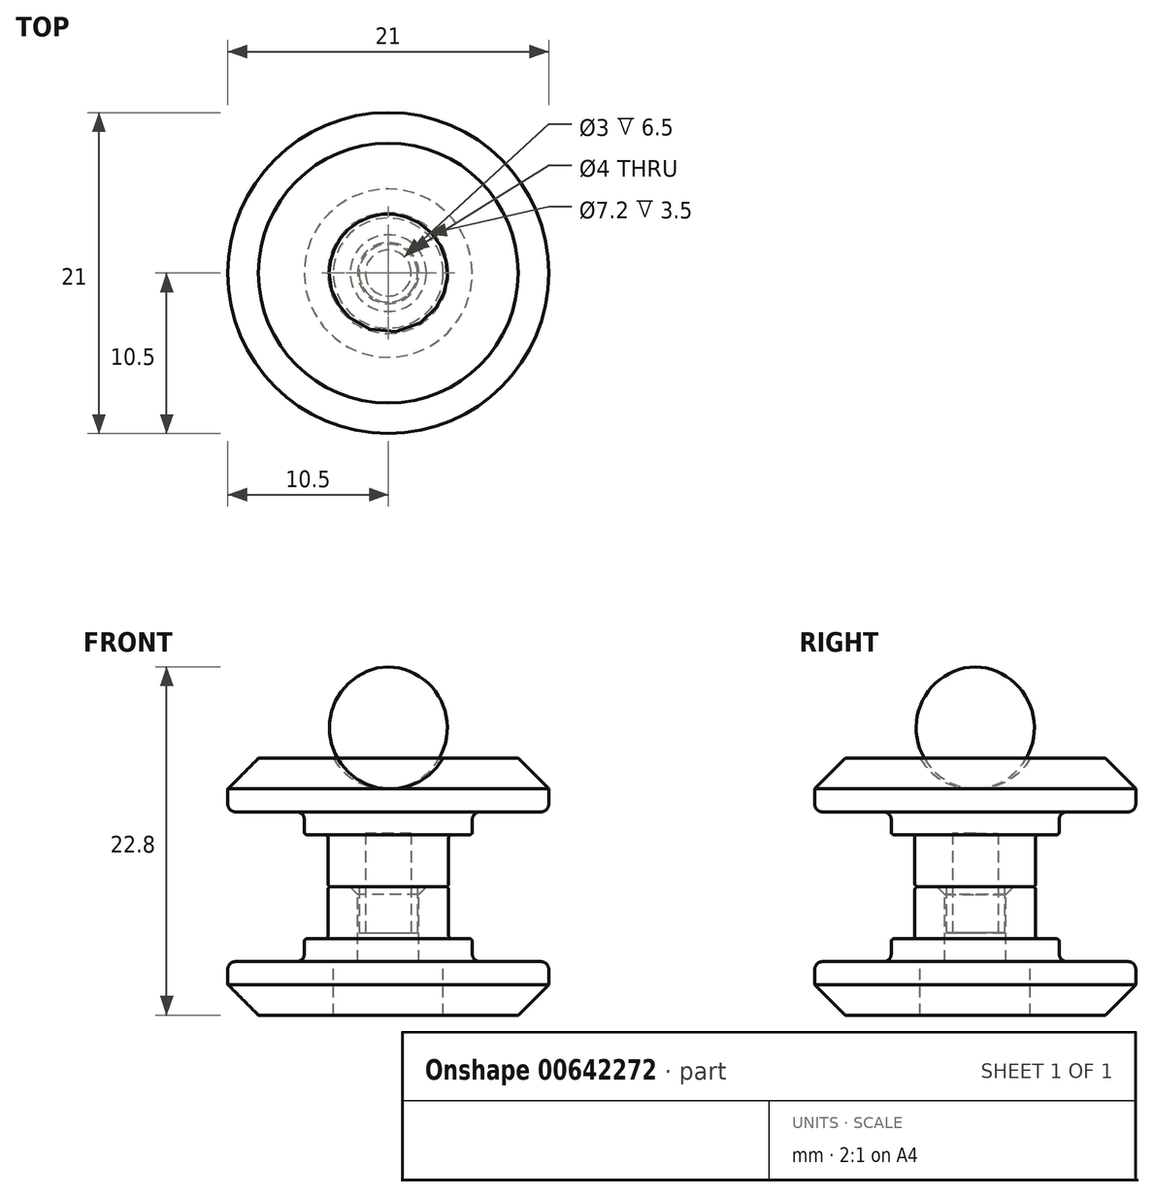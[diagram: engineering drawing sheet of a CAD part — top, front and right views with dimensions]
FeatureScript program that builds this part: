
annotation { "Feature Type Name" : "Feature", "Feature Type Description" : "" }
export const myFeature = defineFeature(function(context is Context, id is Id, definition is map)
    precondition{}
    {
        {
            var Q0;
            Q0=qCreatedBy(makeId("Front.planeOp"),FACE);
            var sketch = newSketch(context, id + "F0", { "sketchPlane" : qUnion([Q0])});
            skCircle(sketch, "E0", {"center": v(0, 0) * mm, "radius": 3.95 * mm, "construction": true});
            skLineSegment(sketch, "E1", {"start": v(0, 0) * mm, "end": v(3.95, 0) * mm});
            skLineSegment(sketch, "E2", {"start": v(3.95, 0) * mm, "end": v(3.95, 3.4) * mm});
            skLineSegment(sketch, "E3", {"start": v(0, 0) * mm, "end": v(0, 3.95) * mm, "construction": true});
            skLineSegment(sketch, "E4.MirrorCS", {"start": v(3.95, 0) * mm, "end": v(3.95, -3.4) * mm});
            skLineSegment(sketch, "E5", {"start": v(3.95, 3.4) * mm, "end": v(0, 3.4) * mm});
            skLineSegment(sketch, "E6", {"start": v(0, 3.4) * mm, "end": v(0, 0) * mm});
            skLineSegment(sketch, "E7.MirrorCS", {"start": v(0, -3.4) * mm, "end": v(0, 0) * mm});
            skLineSegment(sketch, "E8.MirrorCS", {"start": v(3.95, -3.4) * mm, "end": v(0, -3.4) * mm});
            skLineSegment(sketch, "E9", {"start": v(0, -3.4) * mm, "end": v(5.5, -3.4) * mm});
            skLineSegment(sketch, "E10", {"start": v(10.5, -4.9) * mm, "end": v(10.5, -8.4) * mm});
            skLineSegment(sketch, "E11", {"start": v(10.5, -8.4) * mm, "end": v(0, -8.4) * mm});
            skLineSegment(sketch, "E12", {"start": v(0, -8.4) * mm, "end": v(0, -3.4) * mm});
            skLineSegment(sketch, "E13", {"start": v(5.5, -3.4) * mm, "end": v(5.5, -4.9) * mm});
            skLineSegment(sketch, "E14", {"start": v(5.5, -4.9) * mm, "end": v(10.5, -4.9) * mm});
            skLineSegment(sketch, "E15.MirrorCS", {"start": v(0, 3.4) * mm, "end": v(5.5, 3.4) * mm});
            skLineSegment(sketch, "E16.MirrorCS", {"start": v(5.5, 3.4) * mm, "end": v(5.5, 4.9) * mm});
            skLineSegment(sketch, "E17.MirrorCS", {"start": v(5.5, 4.9) * mm, "end": v(10.5, 4.9) * mm});
            skLineSegment(sketch, "E18.MirrorCS", {"start": v(10.5, 4.9) * mm, "end": v(10.5, 8.4) * mm});
            skLineSegment(sketch, "E19.MirrorCS", {"start": v(10.5, 8.4) * mm, "end": v(0, 8.4) * mm});
            skLineSegment(sketch, "E20.MirrorCS", {"start": v(0, 8.4) * mm, "end": v(0, 3.4) * mm});
            skLineSegment(sketch, "E21", {"start": v(0, 0) * mm, "end": v(2, 0) * mm, "construction": true});
            skPoint(sketch, "E22.endSnap0", {"position": v(1.98, 0) * mm});
            skLineSegment(sketch, "E23", {"start": v(0, -8.4) * mm, "end": v(3.6, -8.4) * mm, "construction": true});
            skLineSegment(sketch, "E24", {"start": v(3.6, -8.4) * mm, "end": v(3.6, -4.9) * mm});
            skLineSegment(sketch, "E25", {"start": v(3.6, -4.9) * mm, "end": v(0, -4.9) * mm});
            skLineSegment(sketch, "E26", {"start": v(0, -4.9) * mm, "end": v(2, -4.9) * mm, "construction": true});
            skLineSegment(sketch, "E27", {"start": v(2, -4.9) * mm, "end": v(2, 0) * mm});
            skLineSegment(sketch, "E28", {"start": v(0, 8.4) * mm, "end": v(3.6, 8.4) * mm, "construction": true});
            skLineSegment(sketch, "E29", {"start": v(0, 8.4) * mm, "end": v(0, 6.4) * mm, "construction": true});
            skArc(sketch, "E30", {"start": v(0, 6.4) * mm, "mid": v(2.08, 6.9) * mm, "end": v(3.6, 8.4) * mm});
            skSolve(sketch);
        }
        {
            var Q0;
            {var subQ0=sQuery(id+"F0.wireOp",EDGE,"E4.MirrorCS");Q0=makeQuery(id+"F0.imprint","IMPRINT",FACE,{"disambiguationData":[TD([[makeQuery(id+"F0.imprint","IMPRINT",EDGE,{"derivedFrom":subQ0}),-1.0]])]});}
            var Q1;
            Q1=makeQuery(id+"F0.imprint","IMPRINT",FACE,{"disambiguationData":[TD([[makeQuery(id+"F0.imprint","IMPRINT",EDGE,{"derivedFrom":sQuery(id+"F0.wireOp",EDGE,"E10")}),-1.0]])]});
            var Q2;
            Q2=sQuery(id+"F0.wireOp",EDGE,"E6");
            revolve(context, id + "F1", {"entities" : qUnion([Q0, Q1]), "axis" : qUnion([Q2]), "revolveType" : RevolveType.FULL});
        }
        {
            var Q0;
            Q0=makeQuery(id+"F0.imprint","IMPRINT",FACE,{"disambiguationData":[TD([[makeQuery(id+"F0.imprint","IMPRINT",EDGE,{"derivedFrom":sQuery(id+"F0.wireOp",EDGE,"E1")}),1.0]])]});
            var Q1;
            {var subQ0=sQuery(id+"F0.wireOp",EDGE,"E16.MirrorCS");Q1=makeQuery(id+"F0.imprint","IMPRINT",FACE,{"disambiguationData":[TD([[makeQuery(id+"F0.imprint","IMPRINT",EDGE,{"derivedFrom":subQ0}),1.0]])]});}
            var Q2;
            Q2=sQuery(id+"F0.wireOp",EDGE,"E6");
            revolve(context, id + "F2", {"entities" : qUnion([Q0, Q1]), "axis" : qUnion([Q2]), "revolveType" : RevolveType.FULL});
        }
        {
            var Q0;
            Q0=makeQuery(id+"F1.opRevolve","SWEPT_EDGE",EDGE,{"disambiguationData":[OSD([sQuery(id+"F0.wireOp",EDGE,"E10"),sQuery(id+"F0.wireOp",EDGE,"E11")])]});
            var Q1;
            Q1=makeQuery(id+"F2.opRevolve","SWEPT_EDGE",EDGE,{"disambiguationData":[OSD([sQuery(id+"F0.wireOp",EDGE,"E18.MirrorCS"),sQuery(id+"F0.wireOp",EDGE,"E19.MirrorCS")])]});
            chamfer(context, id + "F3", {"entities" : qUnion([Q0, Q1]), "width" : 2 * mm, "tangentPropagation" : true});
        }
        {
            var Q0;
            Q0=makeQuery(id+"F1.opRevolve","SWEPT_EDGE",EDGE,{"disambiguationData":[OSD([sQuery(id+"F0.wireOp",EDGE,"E9"),sQuery(id+"F0.wireOp",EDGE,"E13")])]});
            var Q1;
            Q1=makeQuery(id+"F2.opRevolve","SWEPT_EDGE",EDGE,{"disambiguationData":[OSD([sQuery(id+"F0.wireOp",EDGE,"E15.MirrorCS"),sQuery(id+"F0.wireOp",EDGE,"E16.MirrorCS")])]});
            var Q2;
            Q2=makeQuery(id+"F1.opRevolve","SWEPT_FACE",FACE,{"disambiguationData":[OSD([sQuery(id+"F0.wireOp",EDGE,"E4.MirrorCS")])]});
            var Q3;
            Q3=makeQuery(id+"F2.opRevolve","SWEPT_FACE",FACE,{"disambiguationData":[OSD([sQuery(id+"F0.wireOp",EDGE,"E2")])]});
            fillet(context, id + "F4", {"entities" : qUnion([Q0, Q1, Q2, Q3]), "radius" : .2 * mm, "tangentPropagation" : true, "allowEdgeOverflow" : false});
        }
        {
            var Q0;
            Q0=makeQuery(id+"F1.opRevolve","SWEPT_EDGE",EDGE,{"disambiguationData":[OSD([sQuery(id+"F0.wireOp",EDGE,"E13"),sQuery(id+"F0.wireOp",EDGE,"E14")])]});
            var Q1;
            Q1=makeQuery(id+"F2.opRevolve","SWEPT_EDGE",EDGE,{"disambiguationData":[OSD([sQuery(id+"F0.wireOp",EDGE,"E16.MirrorCS"),sQuery(id+"F0.wireOp",EDGE,"E17.MirrorCS")])]});
            var Q2;
            Q2=makeQuery(id+"F1.opRevolve","SWEPT_EDGE",EDGE,{"disambiguationData":[OSD([sQuery(id+"F0.wireOp",EDGE,"E10"),sQuery(id+"F0.wireOp",EDGE,"E14")])]});
            var Q3;
            Q3=makeQuery(id+"F2.opRevolve","SWEPT_EDGE",EDGE,{"disambiguationData":[OSD([sQuery(id+"F0.wireOp",EDGE,"E17.MirrorCS"),sQuery(id+"F0.wireOp",EDGE,"E18.MirrorCS")])]});
            fillet(context, id + "F5", {"entities" : qUnion([Q0, Q1, Q2, Q3]), "radius" : .5 * mm, "tangentPropagation" : true, "allowEdgeOverflow" : false});
        }
        {
            var Q0;
            Q0=makeQuery(id+"F2.opRevolve","SWEPT_BODY",BODY,{"disambiguationData":[OSD([sQuery(id+"F0.wireOp",EDGE,"E1"),sQuery(id+"F0.wireOp",EDGE,"E2"),sQuery(id+"F0.wireOp",EDGE,"E6"),sQuery(id+"F0.wireOp",EDGE,"E15.MirrorCS"),sQuery(id+"F0.wireOp",EDGE,"E16.MirrorCS"),sQuery(id+"F0.wireOp",EDGE,"E17.MirrorCS"),sQuery(id+"F0.wireOp",EDGE,"E18.MirrorCS"),sQuery(id+"F0.wireOp",EDGE,"E19.MirrorCS"),sQuery(id+"F0.wireOp",EDGE,"E20.MirrorCS")])]});
            transform(context, id + "F6", {"entities" : qUnion([Q0]), "transformType" : TransformType.TRANSLATION_3D, "dx" : 0 * mm, "dy" : 0 * mm, "dz" : 10 * mm, "makeCopy" : false});
        }
        {
            var Q0;
            Q0=qCreatedBy(makeId("Front.planeOp"),FACE);
            var sketch = newSketch(context, id + "F7", { "sketchPlane" : qUnion([Q0])});
            skLineSegment(sketch, "E31.0.0", {"start": v(3.75, 10) * mm, "end": v(-3.75, 10) * mm, "construction": true});
            skLineSegment(sketch, "E32", {"start": v(0, 10) * mm, "end": v(1.9, 10) * mm});
            skLineSegment(sketch, "E33", {"start": v(1.9, 10) * mm, "end": v(1.9, 7) * mm});
            skLineSegment(sketch, "E34", {"start": v(1.9, 7) * mm, "end": v(0, 7) * mm});
            skLineSegment(sketch, "E35", {"start": v(0, 7) * mm, "end": v(0, 10) * mm});
            skLineSegment(sketch, "E36", {"start": v(0, 7) * mm, "end": v(1.5, 7) * mm});
            skLineSegment(sketch, "E37", {"start": v(1.5, 7) * mm, "end": v(1.5, 10) * mm});
            skSolve(sketch);
        }
        {
            var Q0;
            Q0=makeQuery(id+"F1.opRevolve","SWEPT_EDGE",EDGE,{"disambiguationData":[OSD([sQuery(id+"F0.wireOp",EDGE,"E1"),sQuery(id+"F0.wireOp",EDGE,"E22")])]});
            chamfer(context, id + "F8", {"entities" : qUnion([Q0]), "width" : .5 * mm, "tangentPropagation" : true});
        }
        {
            var Q0;
            {var subQ0=sQuery(id+"F7.wireOp",EDGE,"E33");Q0=makeQuery(id+"F7.imprint","IMPRINT",FACE,{"disambiguationData":[TD([[makeQuery(id+"F7.imprint","IMPRINT",EDGE,{"derivedFrom":subQ0}),-1.0]])]});}
            var Q1;
            Q1=sQuery(id+"F7.wireOp",EDGE,"E35");
            revolve(context, id + "F9", {"operationType" : NewBodyOperationType.ADD, "entities" : qUnion([Q0]), "axis" : qUnion([Q1]), "revolveType" : RevolveType.FULL});
        }
        {
            var Q0;
            Q0=makeQuery(id+"F2.opRevolve","SWEPT_BODY",BODY,{"disambiguationData":[OSD([sQuery(id+"F0.wireOp",EDGE,"E1"),sQuery(id+"F0.wireOp",EDGE,"E2"),sQuery(id+"F0.wireOp",EDGE,"E6"),sQuery(id+"F0.wireOp",EDGE,"E15.MirrorCS"),sQuery(id+"F0.wireOp",EDGE,"E16.MirrorCS"),sQuery(id+"F0.wireOp",EDGE,"E17.MirrorCS"),sQuery(id+"F0.wireOp",EDGE,"E18.MirrorCS"),sQuery(id+"F0.wireOp",EDGE,"E19.MirrorCS"),sQuery(id+"F0.wireOp",EDGE,"E20.MirrorCS")])]});
            transform(context, id + "F10", {"entities" : qUnion([Q0]), "transformType" : TransformType.TRANSLATION_3D, "dx" : 0 * mm, "dy" : 0 * mm, "dz" : -10 * mm, "makeCopy" : false});
        }
        {
            var Q0;
            Q0=makeQuery(id+"F9.boolean.opBoolean","SPLIT",FACE,{"disambiguationData":[TD([makeQuery(id+"F9.opRevolve","SWEPT_FACE",FACE,{"disambiguationData":[OSD([sQuery(id+"F7.wireOp",EDGE,"E37")])]})])],"derivedFrom":makeQuery(id+"F2.opRevolve","SWEPT_FACE",FACE,{"disambiguationData":[OSD([sQuery(id+"F0.wireOp",EDGE,"E1")])]})});
            extrude(context, id + "F11", {"entities" : qUnion([Q0]), "operationType" : NewBodyOperationType.REMOVE, "oppositeDirection" : true, "depth" : 3.5 * mm, "offsetDistance" : 25 * mm});
        }
    });
